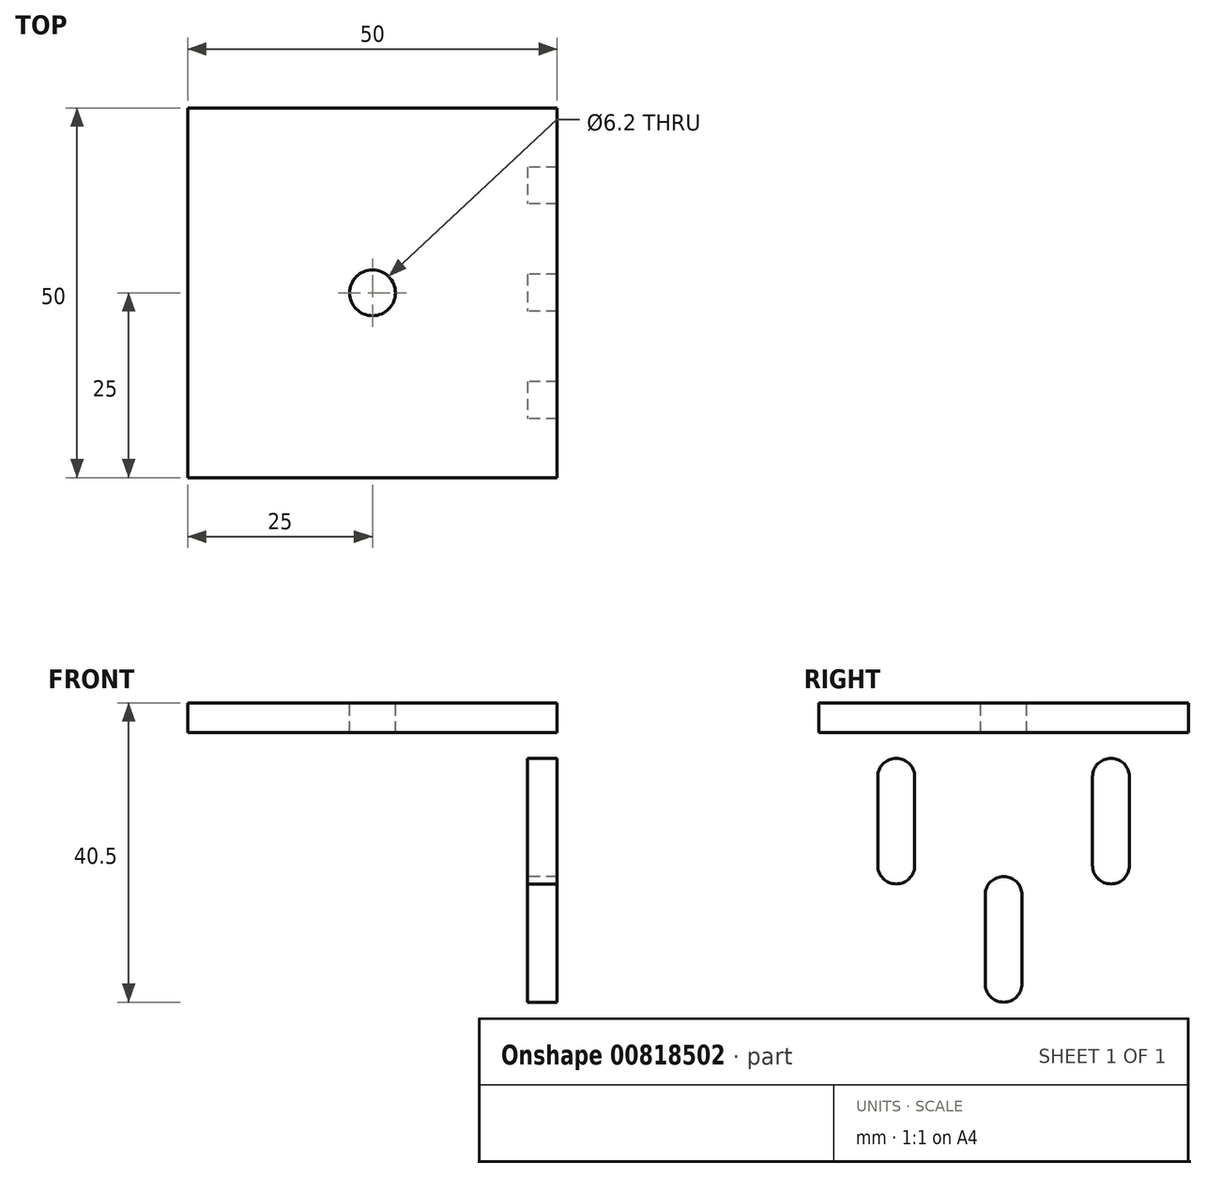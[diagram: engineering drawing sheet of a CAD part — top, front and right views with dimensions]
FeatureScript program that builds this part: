
annotation { "Feature Type Name" : "Feature", "Feature Type Description" : "" }
export const myFeature = defineFeature(function(context is Context, id is Id, definition is map)
    precondition{}
    {
        {
            var Q0;
            Q0=qCreatedBy(makeId("Front.planeOp"),FACE);
            var sketch = newSketch(context, id + "F0", { "sketchPlane" : qUnion([Q0])});
            skLineSegment(sketch, "E0.bottom", {"start": v(0, 0) * mm, "end": v(-50, 0) * mm});
            skLineSegment(sketch, "E0.top", {"start": v(0, -42) * mm, "end": v(-4, -42) * mm});
            skLineSegment(sketch, "E0.left", {"start": v(0, 0) * mm, "end": v(0, -42) * mm});
            skLineSegment(sketch, "E0.right", {"start": v(-50, 0) * mm, "end": v(-50, -4) * mm});
            skLineSegment(sketch, "E1.top", {"start": v(-50, -4) * mm, "end": v(-4, -4) * mm});
            skLineSegment(sketch, "E1.right", {"start": v(-4, -42) * mm, "end": v(-4, -4) * mm});
            skSolve(sketch);
        }
        {
            var Q0;
            Q0=makeQuery(id+"F0.imprint","IMPRINT",FACE,{"disambiguationData":[TD([[makeQuery(id+"F0.imprint","IMPRINT",EDGE,{"derivedFrom":sQuery(id+"F0.wireOp",EDGE,"E0.bottom")}),1.0]])]});
            extrude(context, id + "F1", {"entities" : qUnion([Q0]), "endBound" : BoundingType.SYMMETRIC, "depth" : 50 * mm});
        }
        {
            var Q0;
            Q0=makeQuery(id+"F1.opExtrude","SWEPT_FACE",FACE,{"disambiguationData":[OSD([sQuery(id+"F0.wireOp",EDGE,"E0.bottom")])]});
            var sketch = newSketch(context, id + "F2", { "sketchPlane" : qUnion([Q0])});
            skLineSegment(sketch, "E2", {"start": v(-50, 25) * mm, "end": v(0, -25) * mm, "construction": true});
            skLineSegment(sketch, "E3.bottom", {"start": v(-40.5, 15.5) * mm, "end": v(-9.5, 15.5) * mm, "construction": true});
            skLineSegment(sketch, "E3.top", {"start": v(-40.5, -15.5) * mm, "end": v(-9.5, -15.5) * mm, "construction": true});
            skLineSegment(sketch, "E3.left", {"start": v(-40.5, 15.5) * mm, "end": v(-40.5, -15.5) * mm, "construction": true});
            skLineSegment(sketch, "E3.right", {"start": v(-9.5, 15.5) * mm, "end": v(-9.5, -15.5) * mm, "construction": true});
            skPoint(sketch, "E3.middle", {"position": v(-25, 0) * mm});
            skSolve(sketch);
        }
        {
            var Q0;
            Q0=sQuery(id+"F2.wireOp",VERTEX,"E3.middle");
            var Q1;
            Q1=makeQuery(id+"F1.opExtrude","SWEPT_BODY",BODY,{"disambiguationData":[OSD([sQuery(id+"F0.wireOp",EDGE,"E0.bottom"),sQuery(id+"F0.wireOp",EDGE,"E0.top"),sQuery(id+"F0.wireOp",EDGE,"E0.left"),sQuery(id+"F0.wireOp",EDGE,"E0.right"),sQuery(id+"F0.wireOp",EDGE,"E1.top"),sQuery(id+"F0.wireOp",EDGE,"E1.right")])]});
            hole(context, id + "F3", {"style" : HoleStyle.SIMPLE, "endStyle" : HoleEndStyle.THROUGH, "holeDiameter" : 6.2 * mm, "tappedDepth" : 12 * mm, "tapClearance" : 3, "locations" : qUnion([Q0]), "scope" : qUnion([Q1])});
        }
        {
            var Q0;
            Q0=makeQuery(id+"F1.opExtrude","SWEPT_FACE",FACE,{"disambiguationData":[OSD([sQuery(id+"F0.wireOp",EDGE,"E1.right")])]});
            var sketch = newSketch(context, id + "F4", { "sketchPlane" : qUnion([Q0])});
            skLineSegment(sketch, "E4", {"start": v(0, -38) * mm, "end": v(0, -26) * mm, "construction": true});
            skLineSegment(sketch, "E5", {"start": v(-14.53, -22) * mm, "end": v(-14.53, -10) * mm, "construction": true});
            skLineSegment(sketch, "E6.MirrorCS", {"start": v(14.53, -22) * mm, "end": v(14.53, -10) * mm, "construction": true});
            skArc(sketch, "E7.0.startCap", {"start": v(2.5, -38) * mm, "mid": v(0, -40.5) * mm, "end": v(-2.5, -38) * mm});
            skArc(sketch, "E7.0.endCap", {"start": v(-2.5, -26) * mm, "mid": v(0, -23.5) * mm, "end": v(2.5, -26) * mm});
            skLineSegment(sketch, "E7.0.left", {"start": v(-2.5, -38) * mm, "end": v(-2.5, -26) * mm});
            skLineSegment(sketch, "E7.0.right", {"start": v(2.5, -38) * mm, "end": v(2.5, -26) * mm});
            skArc(sketch, "E7.1.startCap", {"start": v(-12.03, -22) * mm, "mid": v(-14.53, -24.5) * mm, "end": v(-17.03, -22) * mm});
            skArc(sketch, "E7.1.endCap", {"start": v(-17.03, -10) * mm, "mid": v(-14.53, -7.5) * mm, "end": v(-12.03, -10) * mm});
            skLineSegment(sketch, "E7.1.left", {"start": v(-17.03, -22) * mm, "end": v(-17.03, -10) * mm});
            skLineSegment(sketch, "E7.1.right", {"start": v(-12.03, -22) * mm, "end": v(-12.03, -10) * mm});
            skArc(sketch, "E7.2.startCap", {"start": v(17.03, -22) * mm, "mid": v(14.53, -24.5) * mm, "end": v(12.03, -22) * mm});
            skArc(sketch, "E7.2.endCap", {"start": v(12.03, -10) * mm, "mid": v(14.53, -7.5) * mm, "end": v(17.03, -10) * mm});
            skLineSegment(sketch, "E7.2.left", {"start": v(12.03, -22) * mm, "end": v(12.03, -10) * mm});
            skLineSegment(sketch, "E7.2.right", {"start": v(17.03, -22) * mm, "end": v(17.03, -10) * mm});
            skSolve(sketch);
        }
        {
            var Q0;
            Q0=makeQuery(id+"F4.imprint","IMPRINT",FACE,{"disambiguationData":[TD([[makeQuery(id+"F4.imprint","IMPRINT",EDGE,{"derivedFrom":sQuery(id+"F4.wireOp",EDGE,"E7.1.startCap")}),-1.0]])]});
            var Q1;
            Q1=makeQuery(id+"F4.imprint","IMPRINT",FACE,{"disambiguationData":[TD([[makeQuery(id+"F4.imprint","IMPRINT",EDGE,{"derivedFrom":sQuery(id+"F4.wireOp",EDGE,"E7.0.startCap")}),-1.0]])]});
            var Q2;
            Q2=makeQuery(id+"F4.imprint","IMPRINT",FACE,{"disambiguationData":[TD([[makeQuery(id+"F4.imprint","IMPRINT",EDGE,{"derivedFrom":sQuery(id+"F4.wireOp",EDGE,"E7.2.startCap")}),-1.0]])]});
            extrude(context, id + "F5", {"entities" : qUnion([Q0, Q1, Q2]), "operationType" : NewBodyOperationType.REMOVE, "endBound" : BoundingType.THROUGH_ALL, "oppositeDirection" : true, "depth" : 25 * mm});
        }
    });
